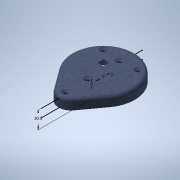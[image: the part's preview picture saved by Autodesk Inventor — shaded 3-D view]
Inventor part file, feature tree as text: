
AUTODESK INVENTOR PART (.ipt)
format: ipt  version: 2020 (Build 240168000, 168)  size: 1,107,968 bytes
history: native  units: mm
features: other x7, sketch x7, extrude x6, plane x3, boolean_combine x3, fillet x2, shell x1, hole x1, split x1, sweep x1, chamfer x1
ambient origin geometry x8: Origin, YZ Plane, XZ Plane, XY Plane, X Axis, Y Axis, Z Axis, Center Point
bodies: Body1 (feature_tree), Body2 (feature_tree), Body3 (feature_tree)
feature tree (33):
  other  "temp case"
  other  "Blocks"
  sketch  "Sketch1"  dims[d2=25.0mm d3=25.0mm]
  extrude  "Extrusion1"  Depth=25.0mm
  extrude  "Extrusion2"  Depth=2.0mm
  fillet  "Fillet2"  Radius=35.355339mm
  shell  "Shell2"  Thickness=2.0mm
  plane  "Work Plane2"
  extrude  "Extrusion6"  Depth=2.0mm TaperAngle=0.0deg
  extrude  "Extrusion7"  Depth=2.0mm
  plane  "Work Plane3"
  hole  "Hole2"  [1 undecoded]
  sketch  "Sketch4"  dims[d21=2.0mm d24=3.5mm]
  other  "Plano de corte"
  split  "Split2"
  plane  "Work Plane5"
  sweep  "Sweep1"
  boolean_combine  "Combine3"
  chamfer  "Chamfer1"  Distance=2.5mm
  extrude  "Extrusion13"  Depth=2.0mm
  boolean_combine  "Combine4"
  boolean_combine  "Combine5"
  fillet  "Fillet5"  Radius=1.5mm
  extrude  "Extrusion15"  Depth=2.0mm TaperAngle=0.0deg
  other  "tapa case"
  sketch  "Sketch2"  dims[d9=2.0mm d10=2.0mm d11=35.355339mm d12=2.0mm]
  sketch  "Sketch3"  dims[d16=12.0mm d17=0.0mm d19=2.0mm d20=0.0mm]
  sketch  "Sketch5"  dims[d25=3.5mm d28=5.0mm]
  sketch  "Sketch6"  dims[d29=5.0mm d30=5.0mm]
  other  "path"
  sketch  "Sketch10"  dims[d36=2.5mm d37=2.5mm d51=4.0mm d52=1.5mm d54=-2.0mm d57=9.0mm d58=0.0mm d68=4.0mm d69=4.0mm d70=4.0mm d71=0.117mm d72=0.0mm d73=-0.117mm d74=1.567mm d75=5.0mm d76=4.0mm d77=2.0mm d78=15.419984mm d79=5.0mm d80=0.0mm d93=4.0mm d94=4.0mm d108=0.0mm d109=0.0mm d110=4.0mm d111=2.0mm d112=45.0deg d128=23.4mm d133=1.95mm d134=1.95mm d135=19.32mm d136=2.0mm d137=30.0mm d138=2.5mm d139=2.5mm d142=6.0mm d143=3.5mm d145=5.0mm d146=10.5mm d147=5.0mm d163=0.35mm d164=180.0deg d165=0.35mm d166=90.0deg d167=5.5mm d168=0.7mm d169=1.5mm d170=0.2mm d171=19.178mm d172=0.0mm d175=2.0mm d176=0.2mm d177=0.0mm d182=2.0mm d183=9.0mm d173=0.5mm d174=0.872665mm]
  other  "back"
  other  "front"
note: 1 required parameter value undecoded (feature->parameter linkage not recoverable at this tier; creation-order binding heuristic only, values carry confidence <= 0.55)
